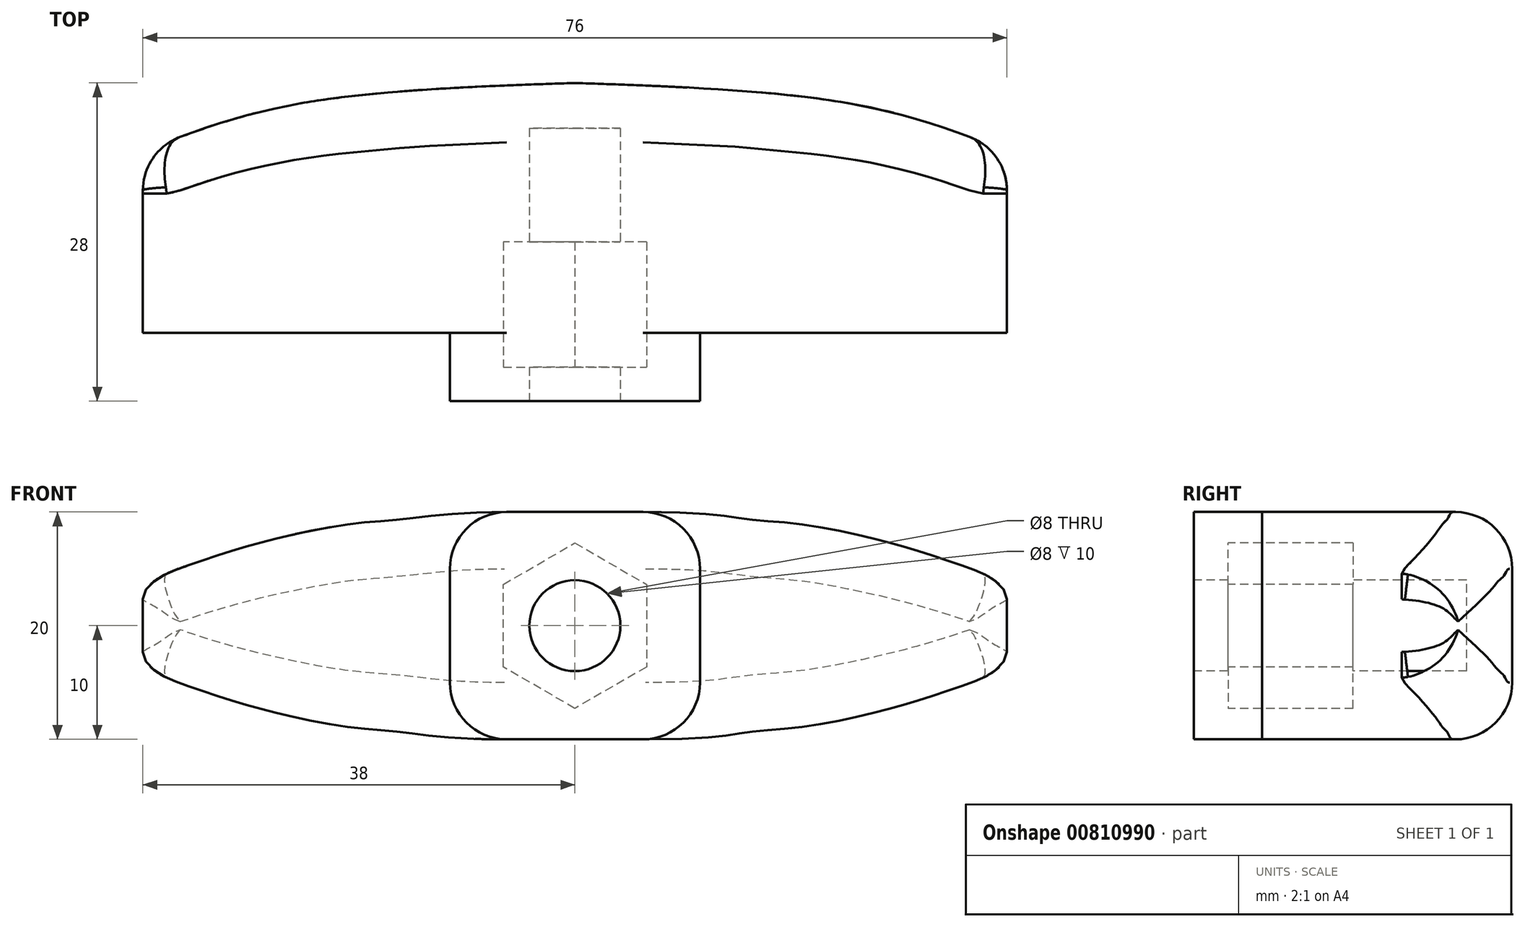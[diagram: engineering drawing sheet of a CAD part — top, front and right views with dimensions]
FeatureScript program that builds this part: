
annotation { "Feature Type Name" : "Feature", "Feature Type Description" : "" }
export const myFeature = defineFeature(function(context is Context, id is Id, definition is map)
    precondition{}
    {
        {
            var Q0;
            Q0=qCreatedBy(makeId("Top.planeOp"),FACE);
            var sketch = newSketch(context, id + "F0", { "sketchPlane" : qUnion([Q0])});
            skLineSegment(sketch, "E0.bottom", {"start": v(-38, 11) * mm, "end": v(38, 11) * mm, "construction": true});
            skLineSegment(sketch, "E0.top", {"start": v(-38, -11) * mm, "end": v(38, -11) * mm, "construction": true});
            skLineSegment(sketch, "E0.left", {"start": v(-38, 11) * mm, "end": v(-38, -11) * mm, "construction": true});
            skLineSegment(sketch, "E0.right", {"start": v(38, 11) * mm, "end": v(38, -11) * mm, "construction": true});
            skPoint(sketch, "E0.middle", {"position": v(0, 0) * mm});
            skLineSegment(sketch, "E1", {"start": v(-38, -11) * mm, "end": v(-43.85, -11) * mm, "construction": true});
            skLineSegment(sketch, "E2", {"start": v(-43.85, -11) * mm, "end": v(-43.85, 5) * mm, "construction": true});
            skLineSegment(sketch, "E3", {"start": v(-43.85, 5) * mm, "end": v(48.5, 5) * mm, "construction": true});
            skLineSegment(sketch, "E4.bottom", {"start": v(11, -22.87) * mm, "end": v(-11, -22.87) * mm, "construction": true});
            skLineSegment(sketch, "E4.top", {"start": v(11, 22.87) * mm, "end": v(-11, 22.87) * mm, "construction": true});
            skLineSegment(sketch, "E4.left", {"start": v(11, -22.87) * mm, "end": v(11, 22.87) * mm, "construction": true});
            skLineSegment(sketch, "E4.right", {"start": v(-11, -22.87) * mm, "end": v(-11, 22.87) * mm, "construction": true});
            skLineSegment(sketch, "E5", {"start": v(-12.58, -11) * mm, "end": v(-12.58, -17) * mm, "construction": true});
            skLineSegment(sketch, "E6", {"start": v(-12.58, -17) * mm, "end": v(16.1, -17) * mm, "construction": true});
            skLineSegment(sketch, "E7", {"start": v(0, 31.77) * mm, "end": v(0, -43.02) * mm, "construction": true});
            skFitSpline(sketch, "E8", {"points": [v(0, 11) * mm, v(-25, 9.04) * mm, v(-38, 5) * mm], "startDerivative": vector(-47.1, -1.64) * mm, "endDerivative": vector(-27.94, -10.82) * mm});
            skLineSegment(sketch, "E9", {"start": v(-38, 5) * mm, "end": v(-38, -11) * mm});
            skLineSegment(sketch, "E10", {"start": v(-11, -11) * mm, "end": v(-11, -17) * mm});
            skLineSegment(sketch, "E11", {"start": v(-11, -17) * mm, "end": v(0, -17) * mm});
            skLineSegment(sketch, "E12", {"start": v(0, -17) * mm, "end": v(0, 11) * mm});
            skLineSegment(sketch, "E13", {"start": v(-38, -11) * mm, "end": v(-11, -11) * mm});
            skFitSpline(sketch, "E14.MirrorCS", {"points": [v(0, 11) * mm, v(25, 9.04) * mm, v(38, 5) * mm], "startDerivative": vector(47.1, -1.64) * mm, "endDerivative": vector(27.94, -10.82) * mm});
            skLineSegment(sketch, "E15.MirrorCS", {"start": v(38, 5) * mm, "end": v(38, -11) * mm});
            skLineSegment(sketch, "E16.MirrorCS", {"start": v(38, -11) * mm, "end": v(11, -11) * mm});
            skLineSegment(sketch, "E17.MirrorCS", {"start": v(12.58, -11) * mm, "end": v(12.58, -17) * mm, "construction": true});
            skLineSegment(sketch, "E18.MirrorCS", {"start": v(11, -17) * mm, "end": v(0, -17) * mm});
            skLineSegment(sketch, "E19.MirrorCS", {"start": v(11, -11) * mm, "end": v(11, -17) * mm});
            skSolve(sketch);
        }
        {
            var Q0;
            Q0 = qSketchRegion(id + "F0", true);
            extrude(context, id + "F1", {"entities" : qUnion([Q0]), "depth" : 10 * mm, "offsetDistance" : 25 * mm, "hasSecondDirection" : true, "secondDirectionOppositeDirection" : true, "secondDirectionDepth" : 10 * mm});
        }
        {
            var Q0;
            Q0=makeQuery(id+"F1.opExtrude","SWEPT_FACE",FACE,{"disambiguationData":[OSD([sQuery(id+"F0.wireOp",EDGE,"E11"),sQuery(id+"F0.wireOp",EDGE,"E18.MirrorCS")])]});
            var sketch = newSketch(context, id + "F2", { "sketchPlane" : qUnion([Q0])});
            skLineSegment(sketch, "E20.bottom", {"start": v(-6.3, 6.3) * mm, "end": v(6.3, 6.3) * mm, "construction": true});
            skLineSegment(sketch, "E20.top", {"start": v(-6.3, -6.3) * mm, "end": v(6.3, -6.3) * mm, "construction": true});
            skLineSegment(sketch, "E20.left", {"start": v(-6.3, 6.3) * mm, "end": v(-6.3, -6.3) * mm, "construction": true});
            skLineSegment(sketch, "E20.right", {"start": v(6.3, 6.3) * mm, "end": v(6.3, -6.3) * mm, "construction": true});
            skPoint(sketch, "E20.middle", {"position": v(0, 0) * mm});
            skLineSegment(sketch, "E21", {"start": v(0, 8.25) * mm, "end": v(0, -14.29) * mm, "construction": true});
            skLineSegment(sketch, "E22", {"start": v(8.15, 0) * mm, "end": v(-22.57, 0) * mm, "construction": true});
            skCircle(sketch, "E23.cCircle", {"center": v(0, 0) * mm, "radius": 6.3 * mm, "construction": true});
            skLineSegment(sketch, "E23.0", {"start": v(-6.3, -3.64) * mm, "end": v(-6.3, 3.64) * mm});
            skLineSegment(sketch, "E23.1", {"start": v(-6.3, 3.64) * mm, "end": v(0, 7.27) * mm});
            skLineSegment(sketch, "E23.2", {"start": v(0, 7.27) * mm, "end": v(6.3, 3.64) * mm});
            skLineSegment(sketch, "E23.3", {"start": v(6.3, 3.64) * mm, "end": v(6.3, -3.64) * mm});
            skLineSegment(sketch, "E23.4", {"start": v(6.3, -3.64) * mm, "end": v(0, -7.27) * mm});
            skLineSegment(sketch, "E23.5", {"start": v(0, -7.27) * mm, "end": v(-6.3, -3.64) * mm});
            skPoint(sketch, "E23.0.midPoint", {"position": v(-6.3, 0) * mm});
            skCircle(sketch, "E24", {"center": v(0, 0) * mm, "radius": 4 * mm});
            skSolve(sketch);
        }
        {
            var Q0;
            Q0=makeQuery(id+"F2.imprint","IMPRINT",FACE,{"disambiguationData":[TD([[makeQuery(id+"F2.imprint","IMPRINT",EDGE,{"derivedFrom":sQuery(id+"F2.wireOp",EDGE,"E23.0")}),-1.0]])]});
            var Q1;
            Q1=makeQuery(id+"F2.imprint","IMPRINT",FACE,{"disambiguationData":[TD([[makeQuery(id+"F2.imprint","IMPRINT",EDGE,{"derivedFrom":sQuery(id+"F2.wireOp",EDGE,"E24")}),1.0]])]});
            extrude(context, id + "F3", {"entities" : qUnion([Q0, Q1]), "operationType" : NewBodyOperationType.REMOVE, "oppositeDirection" : true, "depth" : 14 * mm, "offsetDistance" : 25 * mm});
        }
        {
            var Q0;
            Q0=makeQuery(id+"F2.imprint","IMPRINT",FACE,{"disambiguationData":[TD([[makeQuery(id+"F2.imprint","IMPRINT",EDGE,{"derivedFrom":sQuery(id+"F2.wireOp",EDGE,"E23.0")}),-1.0]])]});
            extrude(context, id + "F4", {"entities" : qUnion([Q0]), "operationType" : NewBodyOperationType.ADD, "oppositeDirection" : true, "depth" : 3 * mm, "offsetDistance" : 25 * mm});
        }
        {
            var Q0;
            Q0=makeQuery(id+"F2.imprint","IMPRINT",FACE,{"disambiguationData":[TD([[makeQuery(id+"F2.imprint","IMPRINT",EDGE,{"derivedFrom":sQuery(id+"F2.wireOp",EDGE,"E24")}),1.0]])]});
            extrude(context, id + "F5", {"entities" : qUnion([Q0]), "operationType" : NewBodyOperationType.REMOVE, "oppositeDirection" : true, "depth" : 24 * mm, "offsetDistance" : 25 * mm});
        }
        {
            var Q0;
            Q0=makeQuery(id+"F1.opExtrude","CAP_EDGE",EDGE,{"disambiguationData":[OSD([sQuery(id+"F0.wireOp",EDGE,"E10")])],"isStart":false});
            var Q1;
            Q1=makeQuery(id+"F1.opExtrude","CAP_EDGE",EDGE,{"disambiguationData":[OSD([sQuery(id+"F0.wireOp",EDGE,"E10")])],"isStart":true});
            var Q2;
            Q2=makeQuery(id+"F1.opExtrude","CAP_EDGE",EDGE,{"disambiguationData":[OSD([sQuery(id+"F0.wireOp",EDGE,"E19.MirrorCS")])],"isStart":true});
            var Q3;
            Q3=makeQuery(id+"F1.opExtrude","CAP_EDGE",EDGE,{"disambiguationData":[OSD([sQuery(id+"F0.wireOp",EDGE,"E19.MirrorCS")])],"isStart":false});
            fillet(context, id + "F6", {"entities" : qUnion([Q0, Q1, Q2, Q3]), "radius" : 5 * mm, "tangentPropagation" : true, "allowEdgeOverflow" : false});
        }
        {
            var Q0;
            Q0=makeQuery(id+"F1.opExtrude","SWEPT_FACE",FACE,{"disambiguationData":[OSD([sQuery(id+"F0.wireOp",EDGE,"E13")])]});
            var sketch = newSketch(context, id + "F7", { "sketchPlane" : qUnion([Q0])});
            skFitSpline(sketch, "E25", {"points": [v(-6, 10) * mm, v(-15.2, 9.37) * mm, v(-20.11, 8.9) * mm, v(-26.02, 7.72) * mm, v(-30.21, 6.57) * mm, v(-34.23, 5.23) * mm, v(-36.86, 4.02) * mm, v(-38, 2.32) * mm], "startDerivative": vector(-66.82, 0) * mm, "endDerivative": vector(0, -20.98) * mm});
            skPoint(sketch, "E26.endSnap0", {"position": v(-38, 0) * mm});
            skLineSegment(sketch, "E27", {"start": v(0, 12.1) * mm, "end": v(0, -14.72) * mm, "construction": true});
            skFitSpline(sketch, "E28.MirrorCS", {"points": [v(-6, -10) * mm, v(-15.2, -9.37) * mm, v(-20.11, -8.9) * mm, v(-26.02, -7.72) * mm, v(-30.21, -6.57) * mm, v(-34.23, -5.23) * mm, v(-36.86, -4.02) * mm, v(-38, -2.32) * mm], "startDerivative": vector(-76, 0) * mm, "endDerivative": vector(0, 20.98) * mm});
            skLineSegment(sketch, "E29", {"start": v(-41.2, 0) * mm, "end": v(42.67, 0) * mm, "construction": true});
            skSolve(sketch);
        }
        {
            var Q0;
            {var subQ1=sQuery(id+"F0.wireOp",EDGE,"E13");var subQ6=makeQuery(id+"F1.opExtrude","CAP_EDGE",EDGE,{"disambiguationData":[OSD([subQ1])],"isStart":false});Q0=makeQuery(id+"F7.imprint","IMPRINT",FACE,{"disambiguationData":[TD([[makeQuery(id+"F7.imprint","IMPRINT",EDGE,{"derivedFrom":subQ6}),-1.0]])]});}
            var Q1;
            {var subQ1=sQuery(id+"F0.wireOp",EDGE,"E13");var subQ6=makeQuery(id+"F1.opExtrude","CAP_EDGE",EDGE,{"disambiguationData":[OSD([subQ1])],"isStart":true});Q1=makeQuery(id+"F7.imprint","IMPRINT",FACE,{"disambiguationData":[TD([[makeQuery(id+"F7.imprint","IMPRINT",EDGE,{"derivedFrom":subQ6}),1.0]])]});}
            extrude(context, id + "F8", {"entities" : qUnion([Q0, Q1]), "operationType" : NewBodyOperationType.REMOVE, "oppositeDirection" : true, "depth" : 25 * mm, "offsetDistance" : 25 * mm});
        }
        {
            var Q0;
            Q0=makeQuery(id+"F1.opExtrude","SWEPT_FACE",FACE,{"disambiguationData":[OSD([sQuery(id+"F0.wireOp",EDGE,"E16.MirrorCS")])]});
            var sketch = newSketch(context, id + "F9", { "sketchPlane" : qUnion([Q0])});
            skFitSpline(sketch, "E30.MirrorCS", {"points": [v(6, 10) * mm, v(15.2, 9.37) * mm, v(20.11, 8.9) * mm, v(26.02, 7.72) * mm, v(30.21, 6.57) * mm, v(34.23, 5.23) * mm, v(36.86, 4.02) * mm, v(38, 2.32) * mm], "startDerivative": vector(87.5, 0) * mm, "endDerivative": vector(0, -20.98) * mm});
            skFitSpline(sketch, "E31.MirrorCS", {"points": [v(6, -10) * mm, v(15.2, -9.37) * mm, v(20.11, -8.9) * mm, v(26.02, -7.72) * mm, v(30.21, -6.57) * mm, v(34.23, -5.23) * mm, v(36.86, -4.02) * mm, v(38, -2.32) * mm], "startDerivative": vector(94.48, 0) * mm, "endDerivative": vector(0, 20.98) * mm});
            skLineSegment(sketch, "E32", {"start": v(-41.2, 0) * mm, "end": v(42.67, 0) * mm, "construction": true});
            skLineSegment(sketch, "E33", {"start": v(0, 14.65) * mm, "end": v(0, -21.42) * mm, "construction": true});
            skSolve(sketch);
        }
        {
            var Q0;
            {var subQ1=sQuery(id+"F0.wireOp",EDGE,"E16.MirrorCS");var subQ6=makeQuery(id+"F1.opExtrude","CAP_EDGE",EDGE,{"disambiguationData":[OSD([subQ1])],"isStart":false});Q0=makeQuery(id+"F9.imprint","IMPRINT",FACE,{"disambiguationData":[TD([[makeQuery(id+"F9.imprint","IMPRINT",EDGE,{"derivedFrom":subQ6}),1.0]])]});}
            var Q1;
            {var subQ1=sQuery(id+"F0.wireOp",EDGE,"E16.MirrorCS");var subQ6=makeQuery(id+"F1.opExtrude","CAP_EDGE",EDGE,{"disambiguationData":[OSD([subQ1])],"isStart":true});Q1=makeQuery(id+"F9.imprint","IMPRINT",FACE,{"disambiguationData":[TD([[makeQuery(id+"F9.imprint","IMPRINT",EDGE,{"derivedFrom":subQ6}),-1.0]])]});}
            extrude(context, id + "F10", {"entities" : qUnion([Q0, Q1]), "operationType" : NewBodyOperationType.REMOVE, "oppositeDirection" : true, "depth" : 25 * mm, "offsetDistance" : 25 * mm});
        }
        {
            var Q0;
            Q0=makeQuery(id+"F1.opExtrude","SWEPT_FACE",FACE,{"disambiguationData":[OSD([sQuery(id+"F0.wireOp",EDGE,"E8")])]});
            var Q1;
            Q1=makeQuery(id+"F1.opExtrude","SWEPT_FACE",FACE,{"disambiguationData":[OSD([sQuery(id+"F0.wireOp",EDGE,"E14.MirrorCS")])]});
            fillet(context, id + "F11", {"entities" : qUnion([Q0, Q1]), "radius" : 5 * mm, "tangentPropagation" : true, "allowEdgeOverflow" : false});
        }
    });
